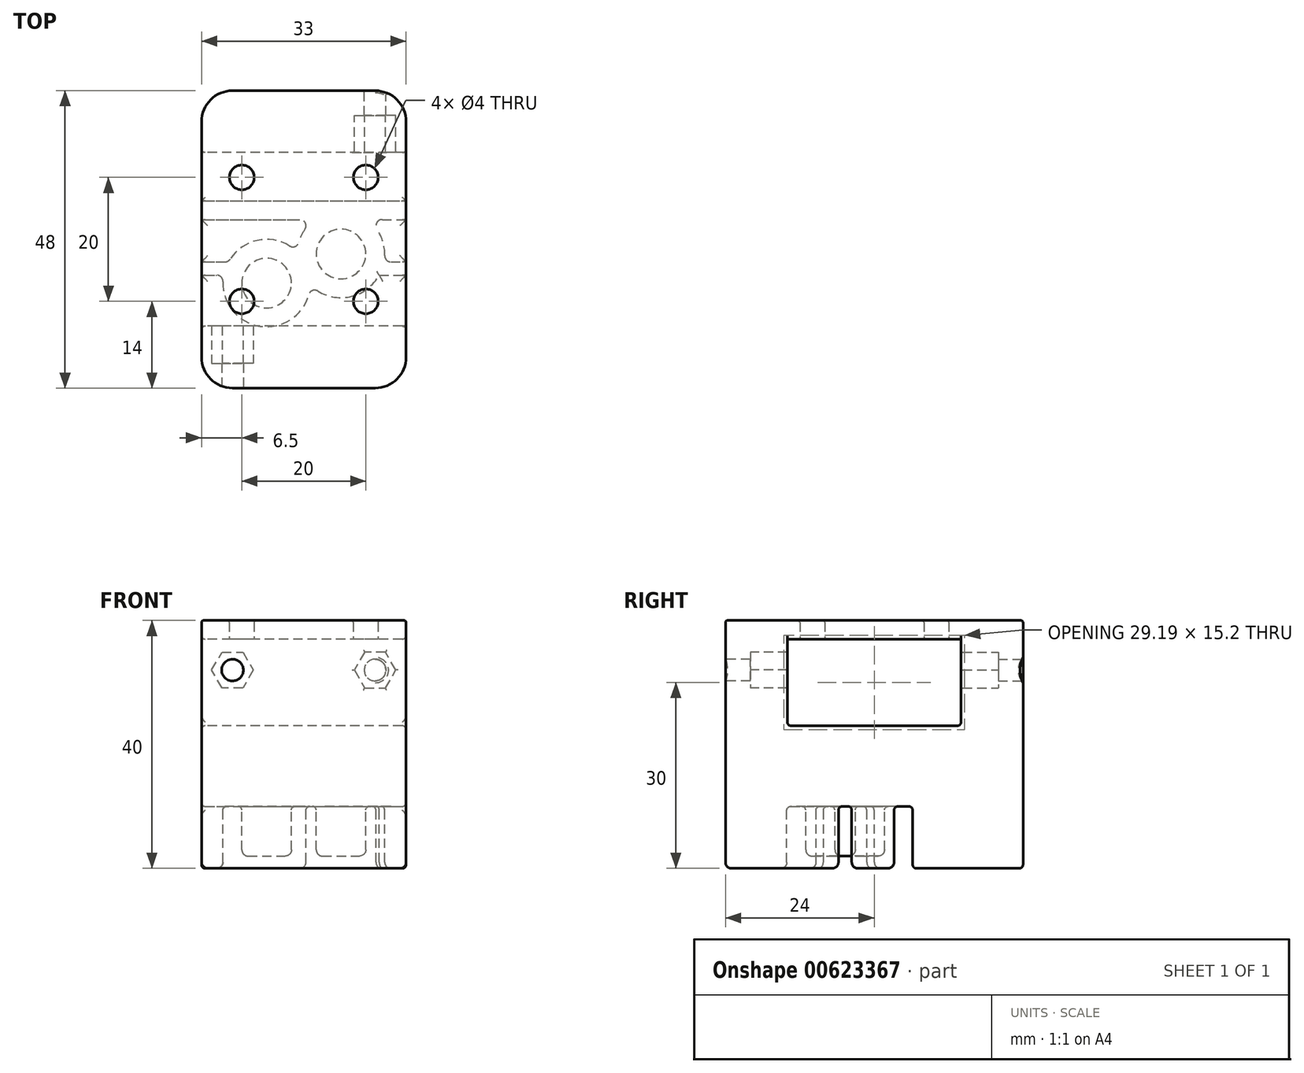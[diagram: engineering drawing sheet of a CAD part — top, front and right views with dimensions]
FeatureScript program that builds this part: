
annotation { "Feature Type Name" : "Feature", "Feature Type Description" : "" }
export const myFeature = defineFeature(function(context is Context, id is Id, definition is map)
    precondition{}
    {
        {
            var Q0;
            Q0=qCreatedBy(makeId("Top.planeOp"),FACE);
            var sketch = newSketch(context, id + "F0", { "sketchPlane" : qUnion([Q0])});
            skCircle(sketch, "E0", {"center": v(0, 0) * mm, "radius": 2 * mm});
            skCircle(sketch, "E1", {"center": v(20, 0) * mm, "radius": 2 * mm});
            skLineSegment(sketch, "E2", {"start": v(0, -10) * mm, "end": v(20, -10) * mm, "construction": true});
            skCircle(sketch, "E3.MirrorC", {"center": v(0, -20) * mm, "radius": 2 * mm});
            skCircle(sketch, "E4.MirrorC", {"center": v(20, -20) * mm, "radius": 2 * mm});
            skLineSegment(sketch, "E5.bottom", {"start": v(26.5, 4) * mm, "end": v(-6.5, 4) * mm});
            skLineSegment(sketch, "E5.top", {"start": v(26.5, -24) * mm, "end": v(-6.5, -24) * mm});
            skLineSegment(sketch, "E5.left", {"start": v(26.5, 4) * mm, "end": v(26.5, -24) * mm});
            skLineSegment(sketch, "E5.right", {"start": v(-6.5, 4) * mm, "end": v(-6.5, -24) * mm});
            skPoint(sketch, "E5.middle", {"position": v(10, -10) * mm});
            skLineSegment(sketch, "E6.bottom", {"start": v(-6.5, 14) * mm, "end": v(26.5, 14) * mm});
            skLineSegment(sketch, "E6.top", {"start": v(-6.5, -34) * mm, "end": v(26.5, -34) * mm});
            skLineSegment(sketch, "E6.left", {"start": v(-6.5, 14) * mm, "end": v(-6.5, -34) * mm});
            skLineSegment(sketch, "E6.right", {"start": v(26.5, 14) * mm, "end": v(26.5, -34) * mm});
            skSolve(sketch);
        }
        {
            var Q0;
            Q0=makeQuery(id+"F0.imprint","IMPRINT",FACE,{"disambiguationData":[TD([[makeQuery(id+"F0.imprint","IMPRINT",EDGE,{"derivedFrom":sQuery(id+"F0.wireOp",EDGE,"E0")}),-1.0]])]});
            var Q1;
            {var subQ0=sQuery(id+"F0.wireOp",EDGE,"E5.bottom");Q1=makeQuery(id+"F0.imprint","IMPRINT",FACE,{"disambiguationData":[TD([[makeQuery(id+"F0.imprint","IMPRINT",EDGE,{"derivedFrom":subQ0}),-1.0]])]});}
            var Q2;
            {var subQ0=sQuery(id+"F0.wireOp",EDGE,"E5.top");Q2=makeQuery(id+"F0.imprint","IMPRINT",FACE,{"disambiguationData":[TD([[makeQuery(id+"F0.imprint","IMPRINT",EDGE,{"derivedFrom":subQ0}),1.0]])]});}
            extrude(context, id + "F1", {"entities" : qUnion([Q0, Q1, Q2]), "depth" : 3 * mm, "offsetDistance" : 25 * mm});
        }
        {
            var Q0;
            {var subQ0=sQuery(id+"F0.wireOp",EDGE,"E5.top");Q0=makeQuery(id+"F0.imprint","IMPRINT",FACE,{"disambiguationData":[TD([[makeQuery(id+"F0.imprint","IMPRINT",EDGE,{"derivedFrom":subQ0}),1.0]])]});}
            var Q1;
            {var subQ0=sQuery(id+"F0.wireOp",EDGE,"E5.bottom");Q1=makeQuery(id+"F0.imprint","IMPRINT",FACE,{"disambiguationData":[TD([[makeQuery(id+"F0.imprint","IMPRINT",EDGE,{"derivedFrom":subQ0}),-1.0]])]});}
            extrude(context, id + "F2", {"entities" : qUnion([Q0, Q1]), "operationType" : NewBodyOperationType.ADD, "oppositeDirection" : true, "depth" : (14) * mm, "offsetDistance" : 25 * mm});
        }
        {
            var Q0;
            Q0=makeQuery(id+"F2.opExtrude","CAP_FACE",FACE,{"disambiguationData":[OSD([sQuery(id+"F0.wireOp",EDGE,"E5.top"),sQuery(id+"F0.wireOp",EDGE,"E6.top"),sQuery(id+"F0.wireOp",EDGE,"E6.left"),sQuery(id+"F0.wireOp",EDGE,"E6.right")])],"isStart":false});
            var sketch = newSketch(context, id + "F3", { "sketchPlane" : qUnion([Q0])});
            skLineSegment(sketch, "E7.bottom", {"start": v(-6.5, 34) * mm, "end": v(26.5, 34) * mm});
            skLineSegment(sketch, "E7.top", {"start": v(-6.5, -14) * mm, "end": v(26.5, -14) * mm});
            skLineSegment(sketch, "E7.left", {"start": v(-6.5, 34) * mm, "end": v(-6.5, -14) * mm});
            skLineSegment(sketch, "E7.right", {"start": v(26.5, 34) * mm, "end": v(26.5, -14) * mm});
            skSolve(sketch);
        }
        {
            var Q0;
            {var subQ0=sQuery(id+"F3.wireOp",EDGE,"E7.top");Q0=makeQuery(id+"F3.imprint","IMPRINT",FACE,{"disambiguationData":[TD([[makeQuery(id+"F3.imprint","IMPRINT",EDGE,{"derivedFrom":subQ0}),1.0]])]});}
            var Q1;
            {var subQ0=sQuery(id+"F3.wireOp",EDGE,"E7.bottom");Q1=makeQuery(id+"F3.imprint","IMPRINT",FACE,{"disambiguationData":[TD([[makeQuery(id+"F3.imprint","IMPRINT",EDGE,{"derivedFrom":subQ0}),-1.0]])]});}
            extrude(context, id + "F4", {"entities" : qUnion([Q0, Q1]), "operationType" : NewBodyOperationType.ADD, "depth" : 13 * mm, "offsetDistance" : 25 * mm});
        }
        {
            var Q0;
            Q0=makeQuery(id+"F4.opExtrude","CAP_FACE",FACE,{"disambiguationData":[OSD([sQuery(id+"F3.wireOp",EDGE,"E7.bottom"),sQuery(id+"F3.wireOp",EDGE,"E7.top"),sQuery(id+"F3.wireOp",EDGE,"E7.left"),sQuery(id+"F3.wireOp",EDGE,"E7.right")])],"isStart":false});
            var sketch = newSketch(context, id + "F5", { "sketchPlane" : qUnion([Q0])});
            skLineSegment(sketch, "E8", {"start": v(26.5, 14.7) * mm, "end": v(-6.5, 14.7) * mm, "construction": true});
            skLineSegment(sketch, "E9", {"start": v(-6.5, 19.4) * mm, "end": v(26.5, 19.4) * mm, "construction": true});
            skLineSegment(sketch, "E10.MirrorCS", {"start": v(-6.5, 10) * mm, "end": v(26.5, 10) * mm, "construction": true});
            skLineSegment(sketch, "E11", {"start": v(10, 14.7) * mm, "end": v(10, 19.4) * mm, "construction": true});
            skLineSegment(sketch, "E12", {"start": v(10, 14.7) * mm, "end": v(10, 10) * mm, "construction": true});
            skCircle(sketch, "E13", {"center": v(16, 12.35) * mm, "radius": 4 * mm});
            skPoint(sketch, "E13.centerSnap0", {"position": v(10, 12.35) * mm});
            skCircle(sketch, "E14", {"center": v(4, 17.05) * mm, "radius": 4 * mm});
            skPoint(sketch, "E14.centerSnap0", {"position": v(10, 17.05) * mm});
            skLineSegment(sketch, "E15", {"start": v(-6.5, 15.77) * mm, "end": v(-2.93, 15.77) * mm});
            skLineSegment(sketch, "E16.MirrorCS", {"start": v(-6.5, 13.62) * mm, "end": v(-2.16, 13.62) * mm});
            skLineSegment(sketch, "E17", {"start": v(0.2, 15.78) * mm, "end": v(7.8, 15.78) * mm, "construction": true});
            skLineSegment(sketch, "E18", {"start": v(7.8, 15.78) * mm, "end": v(10.93, 15.78) * mm, "construction": true});
            skLineSegment(sketch, "E19", {"start": v(1.93, 13.63) * mm, "end": v(6.07, 13.63) * mm, "construction": true});
            skLineSegment(sketch, "E20", {"start": v(6.07, 13.63) * mm, "end": v(10.16, 13.63) * mm, "construction": true});
            skLineSegment(sketch, "E21", {"start": v(12.2, 13.63) * mm, "end": v(19.8, 13.63) * mm, "construction": true});
            skLineSegment(sketch, "E22", {"start": v(19.8, 13.63) * mm, "end": v(22.93, 13.63) * mm, "construction": true});
            skLineSegment(sketch, "E23", {"start": v(18.07, 15.78) * mm, "end": v(22.16, 15.78) * mm, "construction": true});
            skLineSegment(sketch, "E24", {"start": v(13.93, 15.78) * mm, "end": v(18.07, 15.78) * mm, "construction": true});
            skLineSegment(sketch, "E25", {"start": v(-2.93, 15.77) * mm, "end": v(0.2, 15.78) * mm, "construction": true});
            skLineSegment(sketch, "E26", {"start": v(-2.16, 13.62) * mm, "end": v(1.93, 13.63) * mm, "construction": true});
            skLineSegment(sketch, "E27", {"start": v(10.93, 15.78) * mm, "end": v(13.93, 15.78) * mm, "construction": true});
            skLineSegment(sketch, "E28", {"start": v(10.16, 13.63) * mm, "end": v(12.2, 13.63) * mm, "construction": true});
            skLineSegment(sketch, "E29", {"start": v(22.16, 15.78) * mm, "end": v(26.5, 15.78) * mm});
            skLineSegment(sketch, "E30", {"start": v(22.93, 13.63) * mm, "end": v(26.5, 13.63) * mm});
            skArc(sketch, "E31", {"start": v(-2.16, 13.63) * mm, "mid": v(3, 10.07) * mm, "end": v(8.96, 12.04) * mm});
            skArc(sketch, "E32", {"start": v(-2.93, 15.78) * mm, "mid": v(-2.64, 14.67) * mm, "end": v(-2.16, 13.63) * mm, "construction": true});
            skArc(sketch, "E33", {"start": v(11.04, 17.36) * mm, "mid": v(10.17, 20.46) * mm, "end": v(8, 22.85) * mm});
            skArc(sketch, "E34", {"start": v(8.96, 12.04) * mm, "mid": v(10.56, 14.48) * mm, "end": v(11.04, 17.36) * mm, "construction": true});
            skArc(sketch, "E35", {"start": v(22.16, 15.78) * mm, "mid": v(17, 19.33) * mm, "end": v(11.04, 17.36) * mm});
            skArc(sketch, "E36", {"start": v(22.93, 13.63) * mm, "mid": v(22.64, 14.73) * mm, "end": v(22.16, 15.78) * mm, "construction": true});
            skArc(sketch, "E37", {"start": v(11.04, 17.36) * mm, "mid": v(9.44, 14.92) * mm, "end": v(8.96, 12.04) * mm, "construction": true});
            skArc(sketch, "E38", {"start": v(8.96, 12.04) * mm, "mid": v(9.73, 9.12) * mm, "end": v(11.65, 6.8) * mm});
            skLineSegment(sketch, "E39", {"start": v(-6.5, 5.3) * mm, "end": v(26.5, 5.3) * mm, "construction": true});
            skArc(sketch, "E40.0.startCap", {"start": v(-6.5, 3.8) * mm, "mid": v(-8, 5.3) * mm, "end": v(-6.5, 6.8) * mm});
            skArc(sketch, "E40.0.endCap", {"start": v(26.5, 6.8) * mm, "mid": v(28, 5.3) * mm, "end": v(26.5, 3.8) * mm});
            skLineSegment(sketch, "E40.0.left", {"start": v(-6.5, 6.8) * mm, "end": v(26.5, 6.8) * mm});
            skLineSegment(sketch, "E40.0.right", {"start": v(-6.5, 3.8) * mm, "end": v(26.5, 3.8) * mm});
            skArc(sketch, "E41", {"start": v(11.65, 6.8) * mm, "mid": v(16, 5.3) * mm, "end": v(20.35, 6.8) * mm, "construction": true});
            skArc(sketch, "E42", {"start": v(20.35, 6.8) * mm, "mid": v(22.6, 9.85) * mm, "end": v(22.93, 13.63) * mm});
            skArc(sketch, "E43", {"start": v(0, 22.85) * mm, "mid": v(-2.51, 19.74) * mm, "end": v(-2.93, 15.78) * mm});
            skArc(sketch, "E44", {"start": v(8, 22.85) * mm, "mid": v(4, 24.1) * mm, "end": v(0, 22.85) * mm});
            skPoint(sketch, "E45.0", {"position": v(-6.5, -14) * mm});
            skLineSegment(sketch, "E46", {"start": v(31.77, 14.63) * mm, "end": v(35.73, 14.63) * mm, "construction": true});
            skLineSegment(sketch, "E47", {"start": v(31.77, 5.23) * mm, "end": v(36.47, 5.23) * mm, "construction": true});
            skLineSegment(sketch, "E48", {"start": v(32.07, 9.93) * mm, "end": v(36.89, 9.93) * mm, "construction": true});
            skSolve(sketch);
        }
        {
            var Q0;
            Q0=makeQuery(id+"F5.imprint","IMPRINT",FACE,{"disambiguationData":[TD([[makeQuery(id+"F5.imprint","IMPRINT",EDGE,{"derivedFrom":sQuery(id+"F5.wireOp",EDGE,"E14")}),1.0]])]});
            var Q1;
            Q1=makeQuery(id+"F5.imprint","IMPRINT",FACE,{"disambiguationData":[TD([[makeQuery(id+"F5.imprint","IMPRINT",EDGE,{"derivedFrom":sQuery(id+"F5.wireOp",EDGE,"E13")}),1.0]])]});
            extrude(context, id + "F6", {"entities" : qUnion([Q0, Q1]), "operationType" : NewBodyOperationType.ADD, "depth" : 8 * mm, "offsetDistance" : 25 * mm});
        }
        {
            var Q0;
            {var subQ3=sQuery(id+"F5.wireOp",EDGE,"E15");Q0=makeQuery(id+"F5.imprint","IMPRINT",FACE,{"disambiguationData":[TD([[makeQuery(id+"F5.imprint","IMPRINT",EDGE,{"derivedFrom":subQ3}),1.0]])]});}
            var Q1;
            {var subQ3=sQuery(id+"F5.wireOp",EDGE,"E16.MirrorCS");Q1=makeQuery(id+"F5.imprint","IMPRINT",FACE,{"disambiguationData":[TD([[makeQuery(id+"F5.imprint","IMPRINT",EDGE,{"derivedFrom":subQ3}),-1.0]])]});}
            var Q2;
            {var subQ0=sQuery(id+"F5.wireOp",EDGE,"1eb7e74b-3bbd-4d90-bb6d-615939d71b1c.0.left");Q2=makeQuery(id+"F5.imprint","IMPRINT",FACE,{"disambiguationData":[TD([[makeQuery(id+"F5.imprint","IMPRINT",EDGE,{"derivedFrom":subQ0}),1.0]])]});}
            var Q3;
            {var subQ4=sQuery(id+"F5.wireOp",EDGE,"E29");Q3=makeQuery(id+"F5.imprint","IMPRINT",FACE,{"disambiguationData":[TD([[makeQuery(id+"F5.imprint","IMPRINT",EDGE,{"derivedFrom":subQ4}),1.0]])]});}
            var Q4;
            {var subQ0=sQuery(id+"F5.wireOp",EDGE,"E30");Q4=makeQuery(id+"F5.imprint","IMPRINT",FACE,{"disambiguationData":[TD([[makeQuery(id+"F5.imprint","IMPRINT",EDGE,{"derivedFrom":subQ0}),-1.0]])]});}
            var Q5;
            {var subQ0=sQuery(id+"F5.wireOp",EDGE,"E40.0.right");Q5=makeQuery(id+"F5.imprint","IMPRINT",FACE,{"disambiguationData":[TD([[makeQuery(id+"F5.imprint","IMPRINT",EDGE,{"derivedFrom":subQ0}),-1.0]])]});}
            extrude(context, id + "F7", {"entities" : qUnion([Q0, Q1, Q2, Q3, Q4, Q5]), "operationType" : NewBodyOperationType.ADD, "depth" : 10 * mm, "offsetDistance" : 25 * mm});
        }
        {
            var Q0;
            Q0=makeQuery(id+"F7.opExtrude","SWEPT_EDGE",EDGE,{"disambiguationData":[OSD([sQuery(id+"F5.wireOp",EDGE,"1eb7e74b-3bbd-4d90-bb6d-615939d71b1c.0.right"),sQuery(id+"F5.wireOp",EDGE,"E43")])]});
            var Q1;
            Q1=makeQuery(id+"F7.opExtrude","SWEPT_EDGE",EDGE,{"disambiguationData":[OSD([sQuery(id+"F5.wireOp",EDGE,"E15"),sQuery(id+"F5.wireOp",EDGE,"E43")])]});
            var Q2;
            Q2=makeQuery(id+"F7.opExtrude","SWEPT_EDGE",EDGE,{"disambiguationData":[OSD([sQuery(id+"F5.wireOp",EDGE,"E16.MirrorCS"),sQuery(id+"F5.wireOp",EDGE,"E31")])]});
            var Q3;
            Q3=makeQuery(id+"F7.opExtrude","SWEPT_EDGE",EDGE,{"disambiguationData":[OSD([sQuery(id+"F5.wireOp",EDGE,"E31"),sQuery(id+"F5.wireOp",EDGE,"E38")])]});
            var Q4;
            Q4=makeQuery(id+"F7.opExtrude","SWEPT_EDGE",EDGE,{"disambiguationData":[OSD([sQuery(id+"F5.wireOp",EDGE,"E38"),sQuery(id+"F5.wireOp",EDGE,"E40.0.left")])]});
            var Q5;
            Q5=makeQuery(id+"F7.opExtrude","SWEPT_EDGE",EDGE,{"disambiguationData":[OSD([sQuery(id+"F5.wireOp",EDGE,"E40.0.left"),sQuery(id+"F5.wireOp",EDGE,"E42")])]});
            var Q6;
            Q6=makeQuery(id+"F7.opExtrude","SWEPT_EDGE",EDGE,{"disambiguationData":[OSD([sQuery(id+"F5.wireOp",EDGE,"E30"),sQuery(id+"F5.wireOp",EDGE,"E42")])]});
            var Q7;
            Q7=makeQuery(id+"F7.opExtrude","SWEPT_EDGE",EDGE,{"disambiguationData":[OSD([sQuery(id+"F5.wireOp",EDGE,"E33"),sQuery(id+"F5.wireOp",EDGE,"E35")])]});
            var Q8;
            Q8=makeQuery(id+"F7.opExtrude","SWEPT_EDGE",EDGE,{"disambiguationData":[OSD([sQuery(id+"F5.wireOp",EDGE,"E33"),sQuery(id+"F5.wireOp",EDGE,"1eb7e74b-3bbd-4d90-bb6d-615939d71b1c.0.right")])]});
            var Q9;
            Q9=makeQuery(id+"F7.opExtrude","CAP_FACE",FACE,{"disambiguationData":[OSD([sQuery(id+"F3.wireOp",EDGE,"E7.left"),sQuery(id+"F5.wireOp",EDGE,"E15"),sQuery(id+"F5.wireOp",EDGE,"1eb7e74b-3bbd-4d90-bb6d-615939d71b1c.0.right"),sQuery(id+"F5.wireOp",EDGE,"E43")])],"isStart":false});
            var Q10;
            Q10=makeQuery(id+"F6.opExtrude","CAP_FACE",FACE,{"disambiguationData":[OSD([sQuery(id+"F5.wireOp",EDGE,"E14")])],"isStart":false});
            var Q11;
            Q11=makeQuery(id+"F7.opExtrude","CAP_FACE",FACE,{"disambiguationData":[OSD([sQuery(id+"F3.wireOp",EDGE,"E7.right"),sQuery(id+"F5.wireOp",EDGE,"E29"),sQuery(id+"F5.wireOp",EDGE,"E33"),sQuery(id+"F5.wireOp",EDGE,"E35"),sQuery(id+"F5.wireOp",EDGE,"1eb7e74b-3bbd-4d90-bb6d-615939d71b1c.0.right")])],"isStart":false});
            var Q12;
            Q12=makeQuery(id+"F7.opExtrude","CAP_FACE",FACE,{"disambiguationData":[OSD([sQuery(id+"F3.wireOp",EDGE,"E7.left"),sQuery(id+"F5.wireOp",EDGE,"E16.MirrorCS"),sQuery(id+"F5.wireOp",EDGE,"E31"),sQuery(id+"F5.wireOp",EDGE,"E38"),sQuery(id+"F5.wireOp",EDGE,"E40.0.left")])],"isStart":false});
            var Q13;
            Q13=makeQuery(id+"F6.opExtrude","CAP_FACE",FACE,{"disambiguationData":[OSD([sQuery(id+"F5.wireOp",EDGE,"E13")])],"isStart":false});
            var Q14;
            Q14=makeQuery(id+"F7.opExtrude","CAP_FACE",FACE,{"disambiguationData":[OSD([sQuery(id+"F3.wireOp",EDGE,"E7.right"),sQuery(id+"F5.wireOp",EDGE,"E30"),sQuery(id+"F5.wireOp",EDGE,"E40.0.left"),sQuery(id+"F5.wireOp",EDGE,"E42")])],"isStart":false});
            fillet(context, id + "F8", {"entities" : qUnion([Q0, Q1, Q2, Q3, Q4, Q5, Q6, Q7, Q8, Q9, Q10, Q11, Q12, Q13, Q14]), "radius" : 1 * mm, "tangentPropagation" : true, "allowEdgeOverflow" : false});
        }
        {
            var Q0;
            Q0=makeQuery(id+"F4.opExtrude","CAP_FACE",FACE,{"disambiguationData":[OSD([sQuery(id+"F3.wireOp",EDGE,"E7.bottom"),sQuery(id+"F3.wireOp",EDGE,"E7.top"),sQuery(id+"F3.wireOp",EDGE,"E7.left"),sQuery(id+"F3.wireOp",EDGE,"E7.right")])],"isStart":false});
            var Q1;
            Q1=makeQuery(id+"F6.opExtrude","CAP_FACE",FACE,{"disambiguationData":[OSD([sQuery(id+"F3.wireOp",EDGE,"E7.top"),sQuery(id+"F3.wireOp",EDGE,"E7.left"),sQuery(id+"F3.wireOp",EDGE,"E7.right"),sQuery(id+"F5.wireOp",EDGE,"E40.0.right")])],"isStart":false});
            var Q2;
            Q2=makeQuery(id+"F6.opExtrude","CAP_FACE",FACE,{"disambiguationData":[OSD([sQuery(id+"F3.wireOp",EDGE,"E7.bottom"),sQuery(id+"F3.wireOp",EDGE,"E7.left"),sQuery(id+"F3.wireOp",EDGE,"E7.right"),sQuery(id+"F5.wireOp",EDGE,"1eb7e74b-3bbd-4d90-bb6d-615939d71b1c.0.left")])],"isStart":false});
            var Q3;
            Q3=makeQuery(id+"F7.opExtrude","CAP_FACE",FACE,{"disambiguationData":[OSD([sQuery(id+"F3.wireOp",EDGE,"E7.bottom"),sQuery(id+"F3.wireOp",EDGE,"E7.left"),sQuery(id+"F3.wireOp",EDGE,"E7.right"),sQuery(id+"F5.wireOp",EDGE,"1eb7e74b-3bbd-4d90-bb6d-615939d71b1c.0.left")])],"isStart":false});
            var Q4;
            Q4=makeQuery(id+"F7.opExtrude","CAP_FACE",FACE,{"disambiguationData":[OSD([sQuery(id+"F3.wireOp",EDGE,"E7.top"),sQuery(id+"F3.wireOp",EDGE,"E7.left"),sQuery(id+"F3.wireOp",EDGE,"E7.right"),sQuery(id+"F5.wireOp",EDGE,"E40.0.right")])],"isStart":false});
            fillet(context, id + "F9", {"entities" : qUnion([Q0, Q1, Q2, Q3, Q4]), "radius" : 0.6 * mm, "tangentPropagation" : true, "allowEdgeOverflow" : false});
        }
        {
            var Q0;
            Q0=makeQuery(id+"F1.opExtrude","CAP_FACE",FACE,{"disambiguationData":[OSD([sQuery(id+"F0.wireOp",EDGE,"E0"),sQuery(id+"F0.wireOp",EDGE,"E1"),sQuery(id+"F0.wireOp",EDGE,"E3.MirrorC"),sQuery(id+"F0.wireOp",EDGE,"E4.MirrorC"),sQuery(id+"F0.wireOp",EDGE,"E6.bottom"),sQuery(id+"F0.wireOp",EDGE,"E6.top"),sQuery(id+"F0.wireOp",EDGE,"E6.left"),sQuery(id+"F0.wireOp",EDGE,"E6.right")])],"isStart":false});
            fillet(context, id + "F10", {"entities" : qUnion([Q0]), "radius" : 0.3 * mm, "tangentPropagation" : true, "allowEdgeOverflow" : false});
        }
        {
            var Q0;
            {var subQ0=sQuery(id+"F3.wireOp",EDGE,"E7.left");var subQ1=sQuery(id+"F3.wireOp",EDGE,"E7.top");var subQ2=sQuery(id+"F0.wireOp",EDGE,"E6.left");var subQ3=sQuery(id+"F0.wireOp",EDGE,"E6.bottom");Q0=makeQuery(id+"F7.boolean.opBoolean","MERGE",EDGE,{"derivedFrom":[makeQuery(id+"F4.boolean.opBoolean","MERGE",EDGE,{"derivedFrom":[makeQuery(id+"F2.boolean.opBoolean","MERGE",EDGE,{"derivedFrom":[makeQuery(id+"F1.opExtrude","SWEPT_EDGE",EDGE,{"disambiguationData":[OSD([subQ3,subQ2])]}),makeQuery(id+"F2.opExtrude","SWEPT_EDGE",EDGE,{"disambiguationData":[OSD([subQ3,subQ2])]})]}),makeQuery(id+"F4.opExtrude","SWEPT_EDGE",EDGE,{"disambiguationData":[OSD([subQ1,subQ0])]})]}),makeQuery(id+"F7.opExtrude","SWEPT_EDGE",EDGE,{"disambiguationData":[OSD([subQ1,subQ0])]})]});}
            var Q1;
            {var subQ0=sQuery(id+"F3.wireOp",EDGE,"E7.right");var subQ1=sQuery(id+"F3.wireOp",EDGE,"E7.top");var subQ2=sQuery(id+"F0.wireOp",EDGE,"E6.right");var subQ3=sQuery(id+"F0.wireOp",EDGE,"E6.bottom");Q1=makeQuery(id+"F7.boolean.opBoolean","MERGE",EDGE,{"derivedFrom":[makeQuery(id+"F4.boolean.opBoolean","MERGE",EDGE,{"derivedFrom":[makeQuery(id+"F2.boolean.opBoolean","MERGE",EDGE,{"derivedFrom":[makeQuery(id+"F1.opExtrude","SWEPT_EDGE",EDGE,{"disambiguationData":[OSD([subQ3,subQ2])]}),makeQuery(id+"F2.opExtrude","SWEPT_EDGE",EDGE,{"disambiguationData":[OSD([subQ3,subQ2])]})]}),makeQuery(id+"F4.opExtrude","SWEPT_EDGE",EDGE,{"disambiguationData":[OSD([subQ1,subQ0])]})]}),makeQuery(id+"F7.opExtrude","SWEPT_EDGE",EDGE,{"disambiguationData":[OSD([subQ1,subQ0])]})]});}
            var Q2;
            {var subQ0=sQuery(id+"F3.wireOp",EDGE,"E7.right");var subQ1=sQuery(id+"F3.wireOp",EDGE,"E7.bottom");var subQ2=sQuery(id+"F0.wireOp",EDGE,"E6.right");var subQ3=sQuery(id+"F0.wireOp",EDGE,"E6.top");Q2=makeQuery(id+"F7.boolean.opBoolean","MERGE",EDGE,{"derivedFrom":[makeQuery(id+"F4.boolean.opBoolean","MERGE",EDGE,{"derivedFrom":[makeQuery(id+"F2.boolean.opBoolean","MERGE",EDGE,{"derivedFrom":[makeQuery(id+"F1.opExtrude","SWEPT_EDGE",EDGE,{"disambiguationData":[OSD([subQ3,subQ2])]}),makeQuery(id+"F2.opExtrude","SWEPT_EDGE",EDGE,{"disambiguationData":[OSD([subQ3,subQ2])]})]}),makeQuery(id+"F4.opExtrude","SWEPT_EDGE",EDGE,{"disambiguationData":[OSD([subQ1,subQ0])]})]}),makeQuery(id+"F7.opExtrude","SWEPT_EDGE",EDGE,{"disambiguationData":[OSD([subQ1,subQ0])]})]});}
            var Q3;
            {var subQ0=sQuery(id+"F3.wireOp",EDGE,"E7.left");var subQ1=sQuery(id+"F3.wireOp",EDGE,"E7.bottom");var subQ2=sQuery(id+"F0.wireOp",EDGE,"E6.left");var subQ3=sQuery(id+"F0.wireOp",EDGE,"E6.top");Q3=makeQuery(id+"F7.boolean.opBoolean","MERGE",EDGE,{"derivedFrom":[makeQuery(id+"F4.boolean.opBoolean","MERGE",EDGE,{"derivedFrom":[makeQuery(id+"F2.boolean.opBoolean","MERGE",EDGE,{"derivedFrom":[makeQuery(id+"F1.opExtrude","SWEPT_EDGE",EDGE,{"disambiguationData":[OSD([subQ3,subQ2])]}),makeQuery(id+"F2.opExtrude","SWEPT_EDGE",EDGE,{"disambiguationData":[OSD([subQ3,subQ2])]})]}),makeQuery(id+"F4.opExtrude","SWEPT_EDGE",EDGE,{"disambiguationData":[OSD([subQ1,subQ0])]})]}),makeQuery(id+"F7.opExtrude","SWEPT_EDGE",EDGE,{"disambiguationData":[OSD([subQ1,subQ0])]})]});}
            fillet(context, id + "F11", {"entities" : qUnion([Q0, Q1, Q2, Q3]), "radius" : 5 * mm, "tangentPropagation" : true, "allowEdgeOverflow" : false});
        }
        {
            var Q0;
            Q0=makeQuery(id+"F4.opExtrude","CAP_FACE",FACE,{"disambiguationData":[OSD([sQuery(id+"F3.wireOp",EDGE,"E7.bottom"),sQuery(id+"F3.wireOp",EDGE,"E7.top"),sQuery(id+"F3.wireOp",EDGE,"E7.left"),sQuery(id+"F3.wireOp",EDGE,"E7.right")])],"isStart":true});
            var Q1;
            Q1=makeQuery(id+"F1.opExtrude","CAP_EDGE",EDGE,{"disambiguationData":[OSD([sQuery(id+"F0.wireOp",EDGE,"E6.left")])],"isStart":true});
            var Q2;
            Q2=makeQuery(id+"F1.opExtrude","CAP_EDGE",EDGE,{"disambiguationData":[OSD([sQuery(id+"F0.wireOp",EDGE,"E6.right")])],"isStart":true});
            var Q3;
            Q3=makeQuery(id+"F2.opExtrude","CAP_EDGE",EDGE,{"disambiguationData":[OSD([sQuery(id+"F0.wireOp",EDGE,"E5.bottom")])],"isStart":true});
            var Q4;
            Q4=makeQuery(id+"F2.opExtrude","CAP_EDGE",EDGE,{"disambiguationData":[OSD([sQuery(id+"F0.wireOp",EDGE,"E5.top")])],"isStart":true});
            fillet(context, id + "F12", {"entities" : qUnion([Q0, Q1, Q2, Q3, Q4]), "radius" : 0.6 * mm, "tangentPropagation" : true, "allowEdgeOverflow" : false});
        }
        {
            var Q0;
            {var subQ0=sQuery(id+"F3.wireOp",EDGE,"E7.bottom");var subQ1=sQuery(id+"F0.wireOp",EDGE,"E6.top");Q0=makeQuery(id+"F7.boolean.opBoolean","MERGE",FACE,{"derivedFrom":[makeQuery(id+"F4.boolean.opBoolean","MERGE",FACE,{"derivedFrom":[makeQuery(id+"F2.boolean.opBoolean","MERGE",FACE,{"derivedFrom":[makeQuery(id+"F1.opExtrude","SWEPT_FACE",FACE,{"disambiguationData":[OSD([subQ1])]}),makeQuery(id+"F2.opExtrude","SWEPT_FACE",FACE,{"disambiguationData":[OSD([subQ1])]})]}),makeQuery(id+"F4.opExtrude","SWEPT_FACE",FACE,{"disambiguationData":[OSD([subQ0])]})]}),makeQuery(id+"F7.opExtrude","SWEPT_FACE",FACE,{"disambiguationData":[OSD([subQ0])]})]});}
            var sketch = newSketch(context, id + "F13", { "sketchPlane" : qUnion([Q0])});
            skLineSegment(sketch, "E49", {"start": v(3.91, -10) * mm, "end": v(17.94, -10) * mm, "construction": true});
            skLineSegment(sketch, "E50.0", {"start": v(25.9, 0) * mm, "end": v(-5.9, 0) * mm, "construction": true});
            skLineSegment(sketch, "E51", {"start": v(-1.5, 0) * mm, "end": v(-1.5, -10) * mm, "construction": true});
            skCircle(sketch, "E52.cCircle", {"center": v(-1.5, -5) * mm, "radius": 2.9 * mm, "construction": true});
            skLineSegment(sketch, "E52.0", {"start": v(-3.18, -2.1) * mm, "end": v(0.17, -2.1) * mm});
            skLineSegment(sketch, "E52.1", {"start": v(0.17, -2.1) * mm, "end": v(1.84, -5) * mm});
            skLineSegment(sketch, "E52.2", {"start": v(1.84, -5) * mm, "end": v(0.17, -7.9) * mm});
            skLineSegment(sketch, "E52.3", {"start": v(0.17, -7.9) * mm, "end": v(-3.18, -7.9) * mm});
            skLineSegment(sketch, "E52.4", {"start": v(-3.18, -7.9) * mm, "end": v(-4.86, -5) * mm});
            skLineSegment(sketch, "E52.5", {"start": v(-4.86, -5) * mm, "end": v(-3.18, -2.1) * mm});
            skPoint(sketch, "E52.0.midPoint", {"position": v(-1.5, -2.1) * mm});
            skCircle(sketch, "E53", {"center": v(-1.5, -5) * mm, "radius": 1.75 * mm});
            skSolve(sketch);
        }
        {
            var Q0;
            Q0=makeQuery(id+"F13.imprint","IMPRINT",FACE,{"disambiguationData":[TD([[makeQuery(id+"F13.imprint","IMPRINT",EDGE,{"derivedFrom":sQuery(id+"F13.wireOp",EDGE,"E52.0")}),-1.0]])]});
            var Q1;
            Q1=makeQuery(id+"F13.imprint","IMPRINT",FACE,{"disambiguationData":[TD([[makeQuery(id+"F13.imprint","IMPRINT",EDGE,{"derivedFrom":sQuery(id+"F13.wireOp",EDGE,"E53")}),1.0]])]});
            var Q2;
            Q2=makeQuery(id+"F2.opExtrude","SWEPT_FACE",FACE,{"disambiguationData":[OSD([sQuery(id+"F0.wireOp",EDGE,"E5.top")])]});
            extrude(context, id + "F14", {"entities" : qUnion([Q0, Q1]), "operationType" : NewBodyOperationType.REMOVE, "endBound" : BoundingType.UP_TO_SURFACE, "oppositeDirection" : true, "depth" : 25 * mm, "endBoundEntityFace" : qUnion([Q2]), "offsetDistance" : -2 * mm, "hasSecondDirection" : true, "secondDirectionOppositeDirection" : false, "secondDirectionDepth" : -4 * mm});
        }
        {
            var Q0;
            Q0=makeQuery(id+"F13.imprint","IMPRINT",FACE,{"disambiguationData":[TD([[makeQuery(id+"F13.imprint","IMPRINT",EDGE,{"derivedFrom":sQuery(id+"F13.wireOp",EDGE,"E53")}),1.0]])]});
            extrude(context, id + "F15", {"entities" : qUnion([Q0]), "operationType" : NewBodyOperationType.REMOVE, "oppositeDirection" : true, "depth" : 15.4 * mm, "offsetDistance" : 25 * mm});
        }
        {
            var Q0;
            {var subQ0=sQuery(id+"F3.wireOp",EDGE,"E7.top");var subQ1=sQuery(id+"F0.wireOp",EDGE,"E6.bottom");Q0=makeQuery(id+"F7.boolean.opBoolean","MERGE",FACE,{"derivedFrom":[makeQuery(id+"F4.boolean.opBoolean","MERGE",FACE,{"derivedFrom":[makeQuery(id+"F2.boolean.opBoolean","MERGE",FACE,{"derivedFrom":[makeQuery(id+"F1.opExtrude","SWEPT_FACE",FACE,{"disambiguationData":[OSD([subQ1])]}),makeQuery(id+"F2.opExtrude","SWEPT_FACE",FACE,{"disambiguationData":[OSD([subQ1])]})]}),makeQuery(id+"F4.opExtrude","SWEPT_FACE",FACE,{"disambiguationData":[OSD([subQ0])]})]}),makeQuery(id+"F7.opExtrude","SWEPT_FACE",FACE,{"disambiguationData":[OSD([subQ0])]})]});}
            var sketch = newSketch(context, id + "F16", { "sketchPlane" : qUnion([Q0])});
            skLineSegment(sketch, "E54", {"start": v(-21.5, 0) * mm, "end": v(-21.5, -10) * mm, "construction": true});
            skCircle(sketch, "E55.cCircle", {"center": v(-21.5, -5) * mm, "radius": 2.9 * mm, "construction": true});
            skLineSegment(sketch, "E55.0", {"start": v(-23.17, -2.1) * mm, "end": v(-19.83, -2.1) * mm});
            skLineSegment(sketch, "E55.1", {"start": v(-19.83, -2.1) * mm, "end": v(-18.15, -5) * mm});
            skLineSegment(sketch, "E55.2", {"start": v(-18.15, -5) * mm, "end": v(-19.83, -7.9) * mm});
            skLineSegment(sketch, "E55.3", {"start": v(-19.83, -7.9) * mm, "end": v(-23.17, -7.9) * mm});
            skLineSegment(sketch, "E55.4", {"start": v(-23.17, -7.9) * mm, "end": v(-24.85, -5) * mm});
            skLineSegment(sketch, "E55.5", {"start": v(-24.85, -5) * mm, "end": v(-23.17, -2.1) * mm});
            skPoint(sketch, "E55.0.midPoint", {"position": v(-21.5, -2.1) * mm});
            skCircle(sketch, "E56", {"center": v(-21.5, -5) * mm, "radius": 1.75 * mm});
            skLineSegment(sketch, "E57.0", {"start": v(5.9, 0) * mm, "end": v(-25.9, 0) * mm});
            skSolve(sketch);
        }
        {
            var Q0;
            {var subQ0=sQuery(id+"F16.wireOp",EDGE,"E56");var subQ1=sQuery(id+"F3.wireOp",EDGE,"E7.top");var subQ2=sQuery(id+"F0.wireOp",EDGE,"E6.bottom");var subQ3=sQuery(id+"F3.wireOp",EDGE,"E7.right");var subQ4=sQuery(id+"F0.wireOp",EDGE,"E6.right");var subQ5=makeQuery(id+"F11.opFillet","BLEND_EDGE",EDGE,{"blendedFrom":[makeQuery(id+"F7.boolean.opBoolean","MERGE",EDGE,{"derivedFrom":[makeQuery(id+"F4.boolean.opBoolean","MERGE",EDGE,{"derivedFrom":[makeQuery(id+"F2.boolean.opBoolean","MERGE",EDGE,{"derivedFrom":[makeQuery(id+"F1.opExtrude","SWEPT_EDGE",EDGE,{"disambiguationData":[OSD([subQ2,subQ4])]}),makeQuery(id+"F2.opExtrude","SWEPT_EDGE",EDGE,{"disambiguationData":[OSD([subQ2,subQ4])]})]}),makeQuery(id+"F4.opExtrude","SWEPT_EDGE",EDGE,{"disambiguationData":[OSD([subQ1,subQ3])]})]}),makeQuery(id+"F7.opExtrude","SWEPT_EDGE",EDGE,{"disambiguationData":[OSD([subQ1,subQ3])]})]}),makeQuery(id+"F7.boolean.opBoolean","MERGE",FACE,{"derivedFrom":[makeQuery(id+"F4.boolean.opBoolean","MERGE",FACE,{"derivedFrom":[makeQuery(id+"F2.boolean.opBoolean","MERGE",FACE,{"derivedFrom":[makeQuery(id+"F1.opExtrude","SWEPT_FACE",FACE,{"disambiguationData":[OSD([subQ2])]}),makeQuery(id+"F2.opExtrude","SWEPT_FACE",FACE,{"disambiguationData":[OSD([subQ2])]})]}),makeQuery(id+"F4.opExtrude","SWEPT_FACE",FACE,{"disambiguationData":[OSD([subQ1])]})]}),makeQuery(id+"F7.opExtrude","SWEPT_FACE",FACE,{"disambiguationData":[OSD([subQ1])]})]})],"blendedInto":[makeQuery(id+"F7.boolean.opBoolean","MERGE",FACE,{"derivedFrom":[makeQuery(id+"F4.boolean.opBoolean","MERGE",FACE,{"derivedFrom":[makeQuery(id+"F2.boolean.opBoolean","MERGE",FACE,{"derivedFrom":[makeQuery(id+"F1.opExtrude","SWEPT_FACE",FACE,{"disambiguationData":[OSD([subQ2])]}),makeQuery(id+"F2.opExtrude","SWEPT_FACE",FACE,{"disambiguationData":[OSD([subQ2])]})]}),makeQuery(id+"F4.opExtrude","SWEPT_FACE",FACE,{"disambiguationData":[OSD([subQ1])]})]}),makeQuery(id+"F7.opExtrude","SWEPT_FACE",FACE,{"disambiguationData":[OSD([subQ1])]})]})]});var subQ6=makeQuery(id+"F16.imprint","INTERSECT",VERTEX,{"disambiguationData":[OD(0.0)],"derivedFrom":[subQ5,subQ0]});Q0=makeQuery(id+"F16.imprint","IMPRINT",FACE,{"disambiguationData":[TD([[makeQuery(id+"F16.imprint","IMPRINT",EDGE,{"disambiguationData":[TD([[subQ6,-1.0]])],"derivedFrom":subQ0}),1.0]])]});}
            var Q1;
            {var subQ0=sQuery(id+"F16.wireOp",EDGE,"E56");var subQ1=sQuery(id+"F3.wireOp",EDGE,"E7.top");var subQ2=sQuery(id+"F0.wireOp",EDGE,"E6.bottom");var subQ3=sQuery(id+"F3.wireOp",EDGE,"E7.right");var subQ4=sQuery(id+"F0.wireOp",EDGE,"E6.right");var subQ5=makeQuery(id+"F11.opFillet","BLEND_EDGE",EDGE,{"blendedFrom":[makeQuery(id+"F7.boolean.opBoolean","MERGE",EDGE,{"derivedFrom":[makeQuery(id+"F4.boolean.opBoolean","MERGE",EDGE,{"derivedFrom":[makeQuery(id+"F2.boolean.opBoolean","MERGE",EDGE,{"derivedFrom":[makeQuery(id+"F1.opExtrude","SWEPT_EDGE",EDGE,{"disambiguationData":[OSD([subQ2,subQ4])]}),makeQuery(id+"F2.opExtrude","SWEPT_EDGE",EDGE,{"disambiguationData":[OSD([subQ2,subQ4])]})]}),makeQuery(id+"F4.opExtrude","SWEPT_EDGE",EDGE,{"disambiguationData":[OSD([subQ1,subQ3])]})]}),makeQuery(id+"F7.opExtrude","SWEPT_EDGE",EDGE,{"disambiguationData":[OSD([subQ1,subQ3])]})]}),makeQuery(id+"F7.boolean.opBoolean","MERGE",FACE,{"derivedFrom":[makeQuery(id+"F4.boolean.opBoolean","MERGE",FACE,{"derivedFrom":[makeQuery(id+"F2.boolean.opBoolean","MERGE",FACE,{"derivedFrom":[makeQuery(id+"F1.opExtrude","SWEPT_FACE",FACE,{"disambiguationData":[OSD([subQ2])]}),makeQuery(id+"F2.opExtrude","SWEPT_FACE",FACE,{"disambiguationData":[OSD([subQ2])]})]}),makeQuery(id+"F4.opExtrude","SWEPT_FACE",FACE,{"disambiguationData":[OSD([subQ1])]})]}),makeQuery(id+"F7.opExtrude","SWEPT_FACE",FACE,{"disambiguationData":[OSD([subQ1])]})]})],"blendedInto":[makeQuery(id+"F7.boolean.opBoolean","MERGE",FACE,{"derivedFrom":[makeQuery(id+"F4.boolean.opBoolean","MERGE",FACE,{"derivedFrom":[makeQuery(id+"F2.boolean.opBoolean","MERGE",FACE,{"derivedFrom":[makeQuery(id+"F1.opExtrude","SWEPT_FACE",FACE,{"disambiguationData":[OSD([subQ2])]}),makeQuery(id+"F2.opExtrude","SWEPT_FACE",FACE,{"disambiguationData":[OSD([subQ2])]})]}),makeQuery(id+"F4.opExtrude","SWEPT_FACE",FACE,{"disambiguationData":[OSD([subQ1])]})]}),makeQuery(id+"F7.opExtrude","SWEPT_FACE",FACE,{"disambiguationData":[OSD([subQ1])]})]})]});var subQ6=makeQuery(id+"F16.imprint","INTERSECT",VERTEX,{"disambiguationData":[OD(0.0)],"derivedFrom":[subQ5,subQ0]});Q1=makeQuery(id+"F16.imprint","IMPRINT",FACE,{"disambiguationData":[TD([[makeQuery(id+"F16.imprint","IMPRINT",EDGE,{"disambiguationData":[TD([[subQ6,1.0]])],"derivedFrom":subQ0}),1.0]])]});}
            extrude(context, id + "F17", {"entities" : qUnion([Q0, Q1]), "operationType" : NewBodyOperationType.REMOVE, "oppositeDirection" : true, "depth" : 15 * mm, "offsetDistance" : 25 * mm});
        }
        {
            var Q0;
            {var subQ10=sQuery(id+"F16.wireOp",EDGE,"E55.4");Q0=makeQuery(id+"F16.imprint","IMPRINT",FACE,{"disambiguationData":[TD([[makeQuery(id+"F16.imprint","IMPRINT",EDGE,{"derivedFrom":subQ10}),-1.0]])]});}
            var Q1;
            {var subQ8=sQuery(id+"F16.wireOp",EDGE,"E55.1");Q1=makeQuery(id+"F16.imprint","IMPRINT",FACE,{"disambiguationData":[TD([[makeQuery(id+"F16.imprint","IMPRINT",EDGE,{"derivedFrom":subQ8}),-1.0]])]});}
            extrude(context, id + "F18", {"entities" : qUnion([Q0, Q1]), "operationType" : NewBodyOperationType.REMOVE, "oppositeDirection" : true, "depth" : 13.1 * mm, "offsetDistance" : 25 * mm, "hasSecondDirection" : true, "secondDirectionOppositeDirection" : false, "secondDirectionDepth" : -4 * mm});
        }
        {
            var Q0;
            Q0=makeQuery(id+"FPiKaN0hFhnQNJr_1.1.F14.boolean.opBoolean","INTERSECT",EDGE,{"derivedFrom":[makeQuery(id+"F2.opExtrude","SWEPT_FACE",FACE,{"disambiguationData":[OSD([sQuery(id+"F0.wireOp",EDGE,"E5.bottom")])]}),makeQuery(id+"FPiKaN0hFhnQNJr_1.1.F14.opExtrude","SWEPT_FACE",FACE,{"disambiguationData":[OSD([sQuery(id+"F13.wireOp",EDGE,"E52.5")])]})]});
            var Q1;
            Q1=makeQuery(id+"FPiKaN0hFhnQNJr_1.1.F14.boolean.opBoolean","INTERSECT",EDGE,{"derivedFrom":[makeQuery(id+"F2.opExtrude","SWEPT_FACE",FACE,{"disambiguationData":[OSD([sQuery(id+"F0.wireOp",EDGE,"E5.bottom")])]}),makeQuery(id+"FPiKaN0hFhnQNJr_1.1.F14.opExtrude","SWEPT_FACE",FACE,{"disambiguationData":[OSD([sQuery(id+"F13.wireOp",EDGE,"E52.0")])]})]});
            var Q2;
            Q2=makeQuery(id+"FPiKaN0hFhnQNJr_1.1.F14.boolean.opBoolean","INTERSECT",EDGE,{"derivedFrom":[makeQuery(id+"F2.opExtrude","SWEPT_FACE",FACE,{"disambiguationData":[OSD([sQuery(id+"F0.wireOp",EDGE,"E5.bottom")])]}),makeQuery(id+"FPiKaN0hFhnQNJr_1.1.F14.opExtrude","SWEPT_FACE",FACE,{"disambiguationData":[OSD([sQuery(id+"F13.wireOp",EDGE,"E52.1")])]})]});
            var Q3;
            Q3=makeQuery(id+"FPiKaN0hFhnQNJr_1.1.F14.boolean.opBoolean","INTERSECT",EDGE,{"derivedFrom":[makeQuery(id+"F2.opExtrude","SWEPT_FACE",FACE,{"disambiguationData":[OSD([sQuery(id+"F0.wireOp",EDGE,"E5.bottom")])]}),makeQuery(id+"FPiKaN0hFhnQNJr_1.1.F14.opExtrude","SWEPT_FACE",FACE,{"disambiguationData":[OSD([sQuery(id+"F13.wireOp",EDGE,"E52.2")])]})]});
            var Q4;
            Q4=makeQuery(id+"FPiKaN0hFhnQNJr_1.1.F14.boolean.opBoolean","INTERSECT",EDGE,{"derivedFrom":[makeQuery(id+"F2.opExtrude","SWEPT_FACE",FACE,{"disambiguationData":[OSD([sQuery(id+"F0.wireOp",EDGE,"E5.bottom")])]}),makeQuery(id+"FPiKaN0hFhnQNJr_1.1.F14.opExtrude","SWEPT_FACE",FACE,{"disambiguationData":[OSD([sQuery(id+"F13.wireOp",EDGE,"E52.3")])]})]});
            var Q5;
            Q5=makeQuery(id+"FPiKaN0hFhnQNJr_1.1.F14.boolean.opBoolean","INTERSECT",EDGE,{"derivedFrom":[makeQuery(id+"F2.opExtrude","SWEPT_FACE",FACE,{"disambiguationData":[OSD([sQuery(id+"F0.wireOp",EDGE,"E5.bottom")])]}),makeQuery(id+"FPiKaN0hFhnQNJr_1.1.F14.opExtrude","SWEPT_FACE",FACE,{"disambiguationData":[OSD([sQuery(id+"F13.wireOp",EDGE,"E52.4")])]})]});
            var Q6;
            Q6=makeQuery(id+"F14.boolean.opBoolean","COPY",EDGE,{"derivedFrom":makeQuery(id+"F14.opExtrude","CAP_EDGE",EDGE,{"disambiguationData":[OSD([sQuery(id+"F13.wireOp",EDGE,"E52.1")])],"isStart":false})});
            var Q7;
            Q7=makeQuery(id+"F14.boolean.opBoolean","COPY",EDGE,{"derivedFrom":makeQuery(id+"F14.opExtrude","CAP_EDGE",EDGE,{"disambiguationData":[OSD([sQuery(id+"F13.wireOp",EDGE,"E52.0")])],"isStart":false})});
            var Q8;
            Q8=makeQuery(id+"F14.boolean.opBoolean","COPY",EDGE,{"derivedFrom":makeQuery(id+"F14.opExtrude","CAP_EDGE",EDGE,{"disambiguationData":[OSD([sQuery(id+"F13.wireOp",EDGE,"E52.5")])],"isStart":false})});
            var Q9;
            Q9=makeQuery(id+"F14.boolean.opBoolean","COPY",EDGE,{"derivedFrom":makeQuery(id+"F14.opExtrude","CAP_EDGE",EDGE,{"disambiguationData":[OSD([sQuery(id+"F13.wireOp",EDGE,"E52.4")])],"isStart":false})});
            var Q10;
            Q10=makeQuery(id+"F14.boolean.opBoolean","COPY",EDGE,{"derivedFrom":makeQuery(id+"F14.opExtrude","CAP_EDGE",EDGE,{"disambiguationData":[OSD([sQuery(id+"F13.wireOp",EDGE,"E52.3")])],"isStart":false})});
            var Q11;
            Q11=makeQuery(id+"F14.boolean.opBoolean","COPY",EDGE,{"derivedFrom":makeQuery(id+"F14.opExtrude","CAP_EDGE",EDGE,{"disambiguationData":[OSD([sQuery(id+"F13.wireOp",EDGE,"E52.2")])],"isStart":false})});
            var Q12;
            Q12=makeQuery(id+"FPiKaN0hFhnQNJr_1.1.F15.boolean.opBoolean","COPY",EDGE,{"derivedFrom":makeQuery(id+"FPiKaN0hFhnQNJr_1.1.F15.opExtrude","CAP_EDGE",EDGE,{"disambiguationData":[OSD([sQuery(id+"F13.wireOp",EDGE,"E53")])],"isStart":true})});
            var Q13;
            Q13=makeQuery(id+"F15.boolean.opBoolean","COPY",EDGE,{"derivedFrom":makeQuery(id+"F15.opExtrude","CAP_EDGE",EDGE,{"disambiguationData":[OSD([sQuery(id+"F13.wireOp",EDGE,"E53")])],"isStart":true})});
            var Q14;
            Q14=makeQuery(id+"F17.boolean.opBoolean","INTERSECT",EDGE,{"derivedFrom":[makeQuery(id+"F11.opFillet","BLEND_FACE",FACE,{"disambiguationData":[OSD([sQuery(id+"F0.wireOp",EDGE,"E6.bottom"),sQuery(id+"F0.wireOp",EDGE,"E6.right"),sQuery(id+"F3.wireOp",EDGE,"E7.top"),sQuery(id+"F3.wireOp",EDGE,"E7.right")])]}),makeQuery(id+"F17.opExtrude","SWEPT_FACE",FACE,{"disambiguationData":[OSD([sQuery(id+"F16.wireOp",EDGE,"E56")])]})]});
            var Q15;
            Q15=makeQuery(id+"F17.boolean.opBoolean","COPY",EDGE,{"derivedFrom":makeQuery(id+"F17.opExtrude","CAP_EDGE",EDGE,{"disambiguationData":[OSD([sQuery(id+"F16.wireOp",EDGE,"E56")])],"isStart":true})});
            var Q16;
            Q16=makeQuery(id+"F18.boolean.opBoolean","INTERSECT",EDGE,{"derivedFrom":[makeQuery(id+"F2.opExtrude","SWEPT_FACE",FACE,{"disambiguationData":[OSD([sQuery(id+"F0.wireOp",EDGE,"E5.bottom")])]}),makeQuery(id+"F18.opExtrude","SWEPT_FACE",FACE,{"disambiguationData":[OSD([sQuery(id+"F16.wireOp",EDGE,"E55.3")])]})]});
            var Q17;
            Q17=makeQuery(id+"F18.boolean.opBoolean","INTERSECT",EDGE,{"derivedFrom":[makeQuery(id+"F2.opExtrude","SWEPT_FACE",FACE,{"disambiguationData":[OSD([sQuery(id+"F0.wireOp",EDGE,"E5.bottom")])]}),makeQuery(id+"F18.opExtrude","SWEPT_FACE",FACE,{"disambiguationData":[OSD([sQuery(id+"F16.wireOp",EDGE,"E55.2")])]})]});
            var Q18;
            Q18=makeQuery(id+"F18.boolean.opBoolean","INTERSECT",EDGE,{"derivedFrom":[makeQuery(id+"F2.opExtrude","SWEPT_FACE",FACE,{"disambiguationData":[OSD([sQuery(id+"F0.wireOp",EDGE,"E5.bottom")])]}),makeQuery(id+"F18.opExtrude","SWEPT_FACE",FACE,{"disambiguationData":[OSD([sQuery(id+"F16.wireOp",EDGE,"E55.1")])]})]});
            var Q19;
            Q19=makeQuery(id+"F18.boolean.opBoolean","INTERSECT",EDGE,{"derivedFrom":[makeQuery(id+"F2.opExtrude","SWEPT_FACE",FACE,{"disambiguationData":[OSD([sQuery(id+"F0.wireOp",EDGE,"E5.bottom")])]}),makeQuery(id+"F18.opExtrude","SWEPT_FACE",FACE,{"disambiguationData":[OSD([sQuery(id+"F16.wireOp",EDGE,"E55.0")])]})]});
            var Q20;
            Q20=makeQuery(id+"F18.boolean.opBoolean","INTERSECT",EDGE,{"derivedFrom":[makeQuery(id+"F2.opExtrude","SWEPT_FACE",FACE,{"disambiguationData":[OSD([sQuery(id+"F0.wireOp",EDGE,"E5.bottom")])]}),makeQuery(id+"F18.opExtrude","SWEPT_FACE",FACE,{"disambiguationData":[OSD([sQuery(id+"F16.wireOp",EDGE,"E55.5")])]})]});
            var Q21;
            Q21=makeQuery(id+"F18.boolean.opBoolean","INTERSECT",EDGE,{"derivedFrom":[makeQuery(id+"F2.opExtrude","SWEPT_FACE",FACE,{"disambiguationData":[OSD([sQuery(id+"F0.wireOp",EDGE,"E5.bottom")])]}),makeQuery(id+"F18.opExtrude","SWEPT_FACE",FACE,{"disambiguationData":[OSD([sQuery(id+"F16.wireOp",EDGE,"E55.4")])]})]});
            fillet(context, id + "F19", {"entities" : qUnion([Q0, Q1, Q2, Q3, Q4, Q5, Q6, Q7, Q8, Q9, Q10, Q11, Q12, Q13, Q14, Q15, Q16, Q17, Q18, Q19, Q20, Q21]), "radius" : 0.3 * mm, "tangentPropagation" : true, "allowEdgeOverflow" : false});
        }
    });
